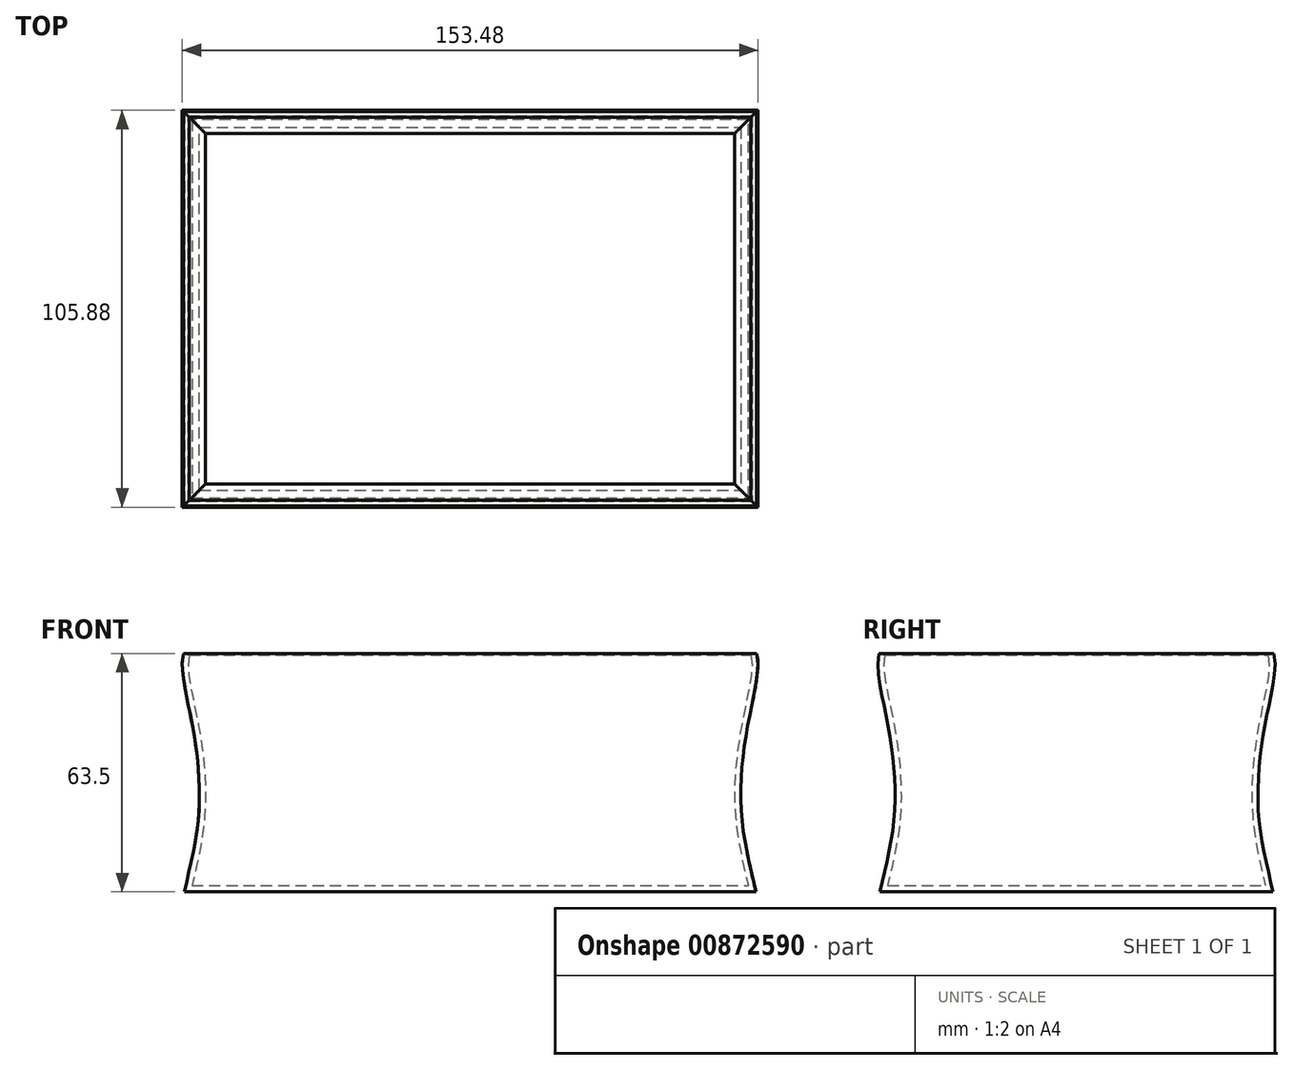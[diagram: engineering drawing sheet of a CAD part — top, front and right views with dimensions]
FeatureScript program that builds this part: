
annotation { "Feature Type Name" : "Feature", "Feature Type Description" : "" }
export const myFeature = defineFeature(function(context is Context, id is Id, definition is map)
    precondition{}
    {
        {
            var Q0;
            Q0=qCreatedBy(makeId("Top.planeOp"),FACE);
            var sketch = newSketch(context, id + "F0", { "sketchPlane" : qUnion([Q0])});
            skLineSegment(sketch, "E0.bottom", {"start": v(-74.6, 50.8) * mm, "end": v(74.6, 50.8) * mm});
            skLineSegment(sketch, "E0.top", {"start": v(-74.6, -50.8) * mm, "end": v(74.6, -50.8) * mm});
            skLineSegment(sketch, "E0.left", {"start": v(-74.6, 50.8) * mm, "end": v(-74.6, -50.8) * mm});
            skLineSegment(sketch, "E0.right", {"start": v(74.6, 50.8) * mm, "end": v(74.6, -50.8) * mm});
            skPoint(sketch, "E0.middle", {"position": v(0, 0) * mm});
            skSolve(sketch);
        }
        {
            var Q0;
            Q0=qCreatedBy(makeId("Front.planeOp"),FACE);
            var sketch = newSketch(context, id + "F1", { "sketchPlane" : qUnion([Q0])});
            skFitSpline(sketch, "E1", {"points": [v(-76.43, 63.5) * mm, v(-73.99, 44.1) * mm, v(-72.25, 22.33) * mm, v(-76.2, 0) * mm], "startDerivative": vector(-10.5, -39.1) * mm, "endDerivative": vector(-21.04, -89.45) * mm});
            skFitSpline(sketch, "E2.0", {"points": [v(-74.88, 63.09) * mm, v(-74.97, 62.77) * mm, v(-75.1, 62.05) * mm, v(-75.18, 60.26) * mm, v(-74.95, 57.48) * mm, v(-74.28, 53.57) * mm, v(-73.54, 50) * mm, v(-72.94, 47.08) * mm, v(-72.5, 44.86) * mm, v(-72.1, 42.65) * mm, v(-71.63, 39.73) * mm, v(-71.15, 36.15) * mm, v(-70.77, 31.98) * mm, v(-70.57, 27.95) * mm, v(-70.56, 24.73) * mm, v(-70.64, 22.25) * mm, v(-70.8, 19.84) * mm, v(-71.1, 16.89) * mm, v(-71.66, 13.26) * mm, v(-72.68, 8.03) * mm, v(-73.77, 3.36) * mm, v(-74.64, -0.37) * mm]});
            skLineSegment(sketch, "E3", {"start": v(-76.43, 63.5) * mm, "end": v(-74.88, 63.09) * mm});
            skLineSegment(sketch, "E4", {"start": v(-76.2, 0) * mm, "end": v(-74.56, 0) * mm});
            skSolve(sketch);
        }
        {
            var Q0;
            Q0=makeQuery(id+"F0.imprint","IMPRINT",FACE,{"disambiguationData":[TD([[makeQuery(id+"F0.imprint","IMPRINT",EDGE,{"derivedFrom":sQuery(id+"F0.wireOp",EDGE,"E0.bottom")}),-1.0]])]});
            extrude(context, id + "F2", {"entities" : qUnion([Q0]), "depth" : 1.6 * mm, "offsetDistance" : 25 * mm});
        }
        {
            var Q0;
            Q0=makeQuery(id+"F1.imprint","IMPRINT",FACE,{"disambiguationData":[TD([[makeQuery(id+"F1.imprint","IMPRINT",EDGE,{"derivedFrom":sQuery(id+"F1.wireOp",EDGE,"E1")}),1.0]])]});
            var Q1;
            Q1=makeQuery(id+"F2.opExtrude","CAP_EDGE",EDGE,{"disambiguationData":[OSD([sQuery(id+"F0.wireOp",EDGE,"E0.left")])],"isStart":false});
            var Q2;
            Q2=makeQuery(id+"F2.opExtrude","CAP_EDGE",EDGE,{"disambiguationData":[OSD([sQuery(id+"F0.wireOp",EDGE,"E0.top")])],"isStart":false});
            var Q3;
            Q3=makeQuery(id+"F2.opExtrude","CAP_EDGE",EDGE,{"disambiguationData":[OSD([sQuery(id+"F0.wireOp",EDGE,"E0.right")])],"isStart":false});
            var Q4;
            Q4=makeQuery(id+"F2.opExtrude","CAP_EDGE",EDGE,{"disambiguationData":[OSD([sQuery(id+"F0.wireOp",EDGE,"E0.bottom")])],"isStart":false});
            sweep(context, id + "F3", {"operationType" : NewBodyOperationType.ADD, "profiles" : qUnion([Q0]), "path" : qUnion([Q1, Q2, Q3, Q4])});
        }
    });
